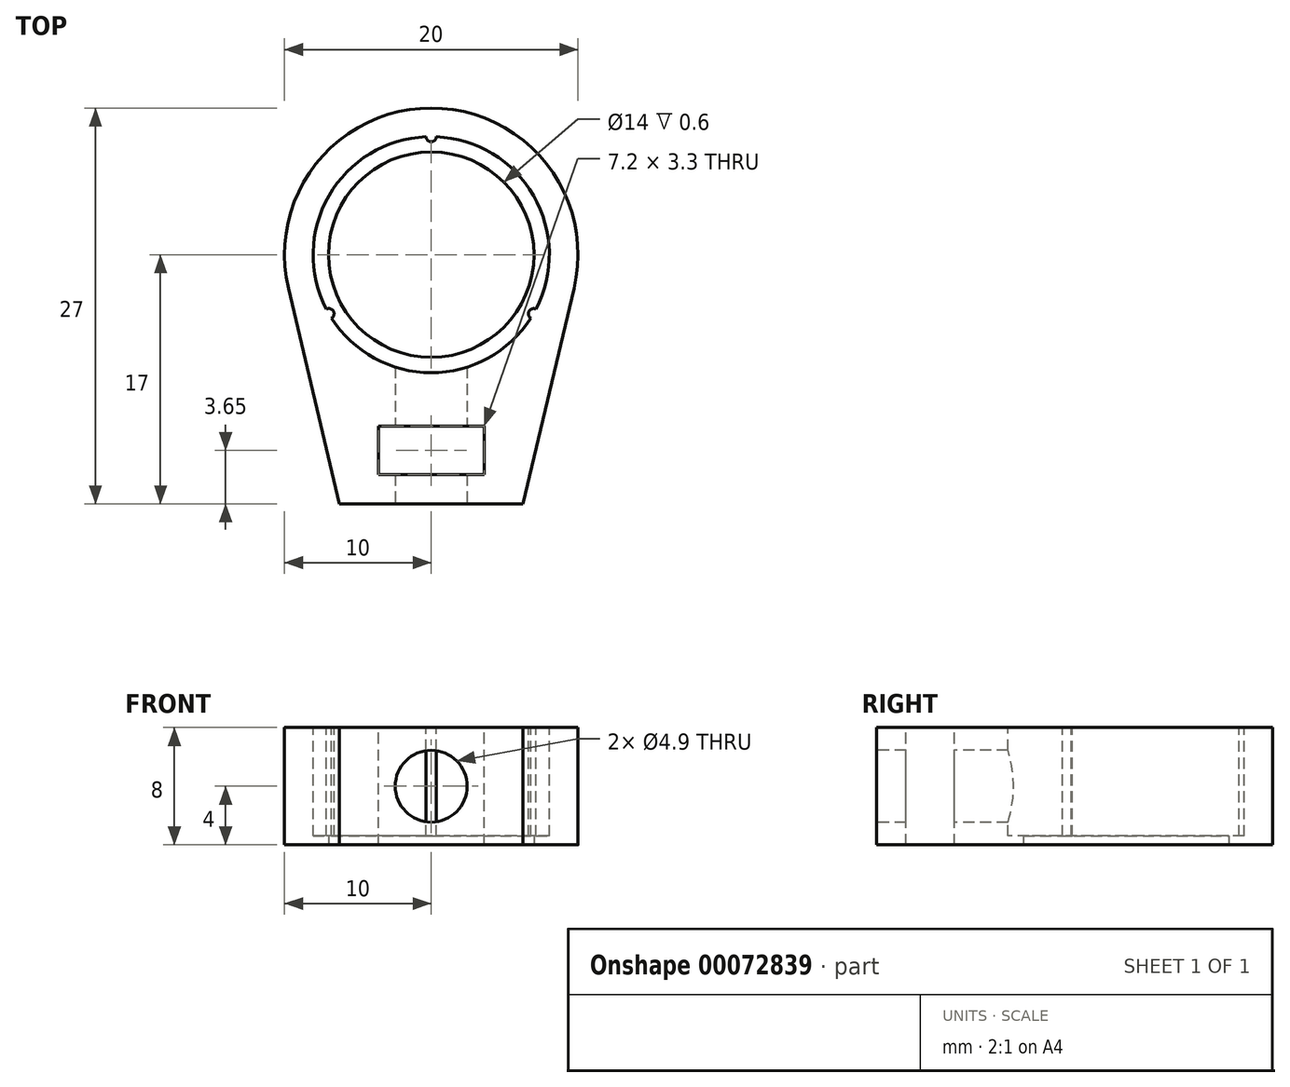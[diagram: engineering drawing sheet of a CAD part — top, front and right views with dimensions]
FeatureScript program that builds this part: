
annotation { "Feature Type Name" : "Feature", "Feature Type Description" : "" }
export const myFeature = defineFeature(function(context is Context, id is Id, definition is map)
    precondition{}
    {
        {
            var Q0;
            Q0=qCreatedBy(makeId("Top.planeOp"),FACE);
            var sketch = newSketch(context, id + "F0", { "sketchPlane" : qUnion([Q0])});
            skCircle(sketch, "E0", {"center": v(0, 0) * mm, "radius": 7 * mm});
            skArc(sketch, "E1", {"start": v(9.73, -2.3) * mm, "mid": v(0, 10) * mm, "end": v(-9.73, -2.3) * mm});
            skLineSegment(sketch, "E2", {"start": v(-9.73, -2.3) * mm, "end": v(-6.25, -17) * mm});
            skLineSegment(sketch, "E3", {"start": v(-6.25, -17) * mm, "end": v(6.25, -17) * mm});
            skLineSegment(sketch, "E4", {"start": v(6.25, -17) * mm, "end": v(9.73, -2.3) * mm});
            skSolve(sketch);
        }
        {
            var Q0;
            Q0 = qSketchRegion(id + "F0", true);
            extrude(context, id + "F1", {"entities" : qUnion([Q0]), "depth" : 8 * mm});
        }
        {
            var Q0;
            Q0=makeQuery(id+"F1.opExtrude","CAP_FACE",FACE,{"disambiguationData":[OSD([sQuery(id+"F0.wireOp",EDGE,"E0"),sQuery(id+"F0.wireOp",EDGE,"E1"),sQuery(id+"F0.wireOp",EDGE,"E2"),sQuery(id+"F0.wireOp",EDGE,"E3"),sQuery(id+"F0.wireOp",EDGE,"E4")])],"isStart":false});
            var sketch = newSketch(context, id + "F2", { "sketchPlane" : qUnion([Q0])});
            skArc(sketch, "E5", {"start": v(-0.35, 8.04) * mm, "mid": v(-6.97, 4.03) * mm, "end": v(-7.14, -3.72) * mm});
            skArc(sketch, "E6", {"start": v(-0.35, 8.04) * mm, "mid": v(0, 7.7) * mm, "end": v(0.35, 8.04) * mm});
            skArc(sketch, "E7", {"start": v(7.14, -3.72) * mm, "mid": v(6.67, -3.85) * mm, "end": v(6.79, -4.32) * mm});
            skArc(sketch, "E8", {"start": v(-6.79, -4.32) * mm, "mid": v(-6.67, -3.85) * mm, "end": v(-7.14, -3.72) * mm});
            skLineSegment(sketch, "E9", {"start": v(0, 0) * mm, "end": v(12.99, -7.5) * mm, "construction": true});
            skLineSegment(sketch, "E10", {"start": v(0, 0) * mm, "end": v(-12.5, -7.22) * mm, "construction": true});
            skArc(sketch, "E11.trimOffspring", {"start": v(7.14, -3.72) * mm, "mid": v(6.97, 4.03) * mm, "end": v(0.35, 8.04) * mm});
            skArc(sketch, "E12.trimOffspring", {"start": v(-6.79, -4.32) * mm, "mid": v(0, -8.05) * mm, "end": v(6.79, -4.32) * mm});
            skSolve(sketch);
        }
        {
            var Q0;
            Q0 = qSketchRegion(id + "F2", true);
            extrude(context, id + "F3", {"entities" : qUnion([Q0]), "operationType" : NewBodyOperationType.REMOVE, "oppositeDirection" : true, "depth" : 7.4 * mm});
        }
        {
            var Q0;
            Q0=makeQuery(id+"F1.opExtrude","SWEPT_FACE",FACE,{"disambiguationData":[OSD([sQuery(id+"F0.wireOp",EDGE,"E3")])]});
            var sketch = newSketch(context, id + "F4", { "sketchPlane" : qUnion([Q0])});
            skCircle(sketch, "E13", {"center": v(0, 4) * mm, "radius": 2.45 * mm});
            skSolve(sketch);
        }
        {
            var Q0;
            Q0 = qSketchRegion(id + "F4", true);
            extrude(context, id + "F5", {"entities" : qUnion([Q0]), "operationType" : NewBodyOperationType.REMOVE, "oppositeDirection" : true, "depth" : 12 * mm});
        }
        {
            var Q0;
            Q0=makeQuery(id+"F1.opExtrude","CAP_FACE",FACE,{"disambiguationData":[OSD([sQuery(id+"F0.wireOp",EDGE,"E0"),sQuery(id+"F0.wireOp",EDGE,"E1"),sQuery(id+"F0.wireOp",EDGE,"E2"),sQuery(id+"F0.wireOp",EDGE,"E3"),sQuery(id+"F0.wireOp",EDGE,"E4")])],"isStart":false});
            var sketch = newSketch(context, id + "F6", { "sketchPlane" : qUnion([Q0])});
            skLineSegment(sketch, "E14.bottom", {"start": v(-3.6, -11.7) * mm, "end": v(3.6, -11.7) * mm});
            skLineSegment(sketch, "E14.top", {"start": v(-3.6, -15) * mm, "end": v(3.6, -15) * mm});
            skLineSegment(sketch, "E14.left", {"start": v(-3.6, -11.7) * mm, "end": v(-3.6, -15) * mm});
            skLineSegment(sketch, "E14.right", {"start": v(3.6, -11.7) * mm, "end": v(3.6, -15) * mm});
            skSolve(sketch);
        }
        {
            var Q0;
            Q0 = qSketchRegion(id + "F6", true);
            extrude(context, id + "F7", {"entities" : qUnion([Q0]), "operationType" : NewBodyOperationType.REMOVE, "endBound" : BoundingType.THROUGH_ALL, "oppositeDirection" : true, "depth" : 25 * mm});
        }
    });
